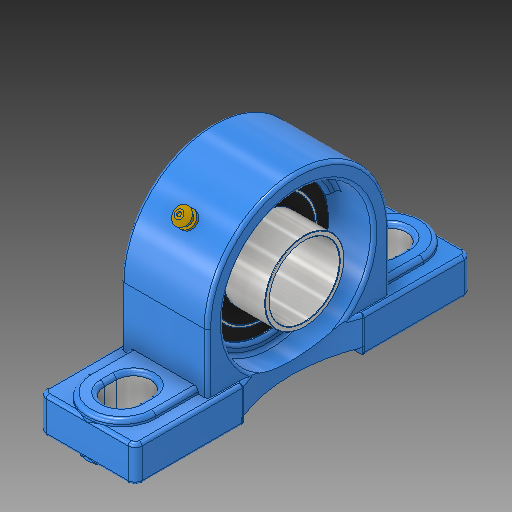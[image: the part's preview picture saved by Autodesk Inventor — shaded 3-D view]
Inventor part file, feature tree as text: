
AUTODESK INVENTOR PART (.ipt)
format: ipt  version: 2019 (Build 230136000, 136)  size: 675,328 bytes
history: native  units: in
note: dims shown in document units (in); Inventor stores cm internally (conversion verified against a paired STEP export)
features: sketch x28, plane x7, other x3
ambient origin geometry x8: Origin, YZ Plane, XZ Plane, XY Plane, X Axis, Y Axis, Z Axis, Center Point
bodies: Solid1 (feature_tree)
feature tree (38):
  other  "Pillow Bearing inventor.ipt"
  other  "Solid1::Pillow Bearing inventor.ipt"
  other  "TaggingFeature1"
  sketch  "Sketch1"  dims[d0=0.3937in]
  sketch  "Sketch2"
  sketch  "Sketch3"
  sketch  "Sketch4"
  sketch  "Sketch5"
  sketch  "Sketch6"
  sketch  "Sketch7"
  sketch  "Sketch8"
  sketch  "Sketch9"
  sketch  "Sketch10"
  sketch  "Sketch11"
  sketch  "Sketch13"
  sketch  "Sketch14"
  sketch  "Sketch15"
  sketch  "Sketch17"
  sketch  "Sketch18"
  sketch  "Sketch19"
  sketch  "Sketch20"
  sketch  "Sketch21"
  sketch  "Sketch22"
  sketch  "Sketch23"
  sketch  "Sketch24"
  sketch  "Sketch25"
  sketch  "Sketch26"
  sketch  "Sketch27"
  sketch  "Sketch28"
  sketch  "Sketch29"
  sketch  "Sketch30"
  plane  "Work Plane1"
  plane  "Work Plane2"
  plane  "Work Plane5"
  plane  "Work Plane6"
  plane  "Work Plane7"
  plane  "Work Plane8"
  plane  "Work Plane9"
